# Revit family: ledlinear-e_cl12-40w-3000-wh-em1_549003003800
name_source: partatom
category: Leuchten
revit_build: Autodesk Revit 2016 (Build: 20190508_0715(x64)
units: mm (PartAtom-declared; Revit-internal decimal feet)

## family parameters
Basisbauteil = Fläche
Beim Laden mit Abzugskörper schneiden = Nein
Bemaßung runder Anschluss = Durchmesser verwenden
Gemeinsam genutzt = Nein
Lichtquelle = Nein
Raumberechnungspunkt = Nein
Teiletyp = Normal

## types (1)
- LEDLinear-E CL12-40W-3000-WH-EM1 (1 x LED, 4320 lm)
    Approval mark = CE
    Beschreibung = Easy to install LED linear solution. Elegant but sturdy design: IP44 and IK06. Comfortable light due to opal diffusor. Central or side power connection. Motion and daylight sensor accessory available.
    CIE Flux Codes = 44 74 92 95 100
    Control Gear = Electronic ballast
    Height = 75 mm
    Hersteller = OPPLE
    Lamp Light Flux = 4320 lm
    Lamp count = 1
    Lampe = 1 x LED
    Length = 180 mm  [stored 0.590551 ft]
    Luminous efficacy = 108 lm/W
    ModVariant = Nein
    Modell = 549003003800
    Mounting Place = Ceiling
    Mounting Type = Surface mounted
    Number of Poles = 1
    OnlyDefault = Ja
    Power Factor = 1
    Product Name = LEDLinear-E CL12-40W-3000-WH-EM1
    Product group = Linear EcoMax
    ProductGroupID = 303
    Protection Class = Protection class I
    Protection Degree = IP 44
    RLX_Detail_Level = 1
    RlxData = <blob elided: 95441 chars, md5=47cf52eb>
    Scheinlast = 40 VA
    Socket = socket
    Standby Power = 0 W
    System Light Flux = 4320 lm
    System Power = 40 W
    Typenbild = 549003003800.jpg
    Typenkommentare = Product without accessories
    URL = http://relux.com
    VarID = ---
    Voltage = 0 V
    Vorgabe-Ansicht = 1800 mm
    Weight = 0.00 kg
    Width = 1200 mm

note: [stored X ft] marks values corroborated as IEEE doubles in the binary element streams (Revit-internal decimal feet)

## geometry (parser evidence)
native form markers: Blend x4, Sweep x14
no freeform markers — native parametric forms only
